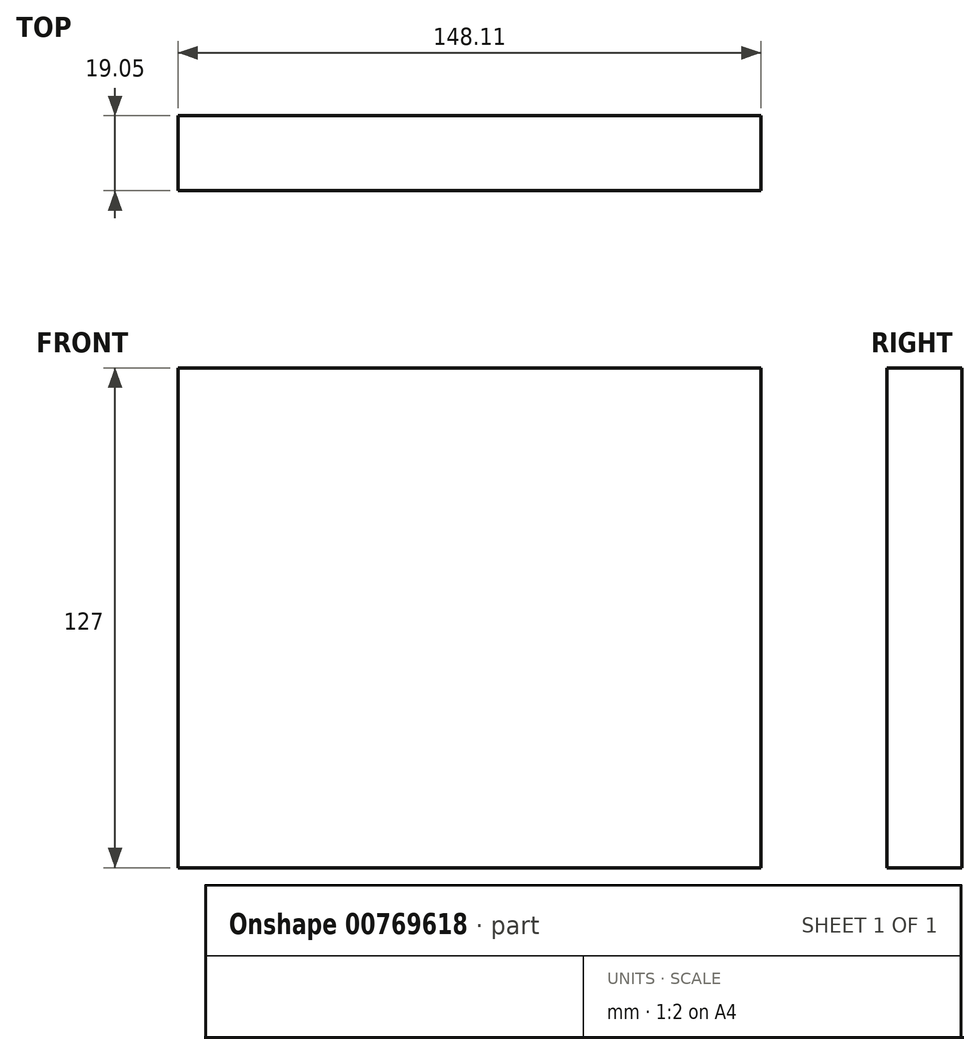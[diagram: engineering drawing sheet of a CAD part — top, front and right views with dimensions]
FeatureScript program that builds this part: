
annotation { "Feature Type Name" : "Feature", "Feature Type Description" : "" }
export const myFeature = defineFeature(function(context is Context, id is Id, definition is map)
    precondition{}
    {
        {
            var Q0;
            Q0=qCreatedBy(makeId("Front.planeOp"),FACE);
            var sketch = newSketch(context, id + "F0", { "sketchPlane" : qUnion([Q0])});
            skLineSegment(sketch, "E0.bottom", {"start": v(-78.1, 47.94) * mm, "end": v(70, 47.94) * mm});
            skLineSegment(sketch, "E0.top", {"start": v(-78.1, -79.06) * mm, "end": v(70, -79.06) * mm});
            skLineSegment(sketch, "E0.left", {"start": v(-78.1, 47.94) * mm, "end": v(-78.1, -79.06) * mm});
            skLineSegment(sketch, "E0.right", {"start": v(70, 47.94) * mm, "end": v(70, -79.06) * mm});
            skSolve(sketch);
        }
        {
            var Q0;
            Q0=makeQuery(id+"F0.imprint","IMPRINT",FACE,{"disambiguationData":[TD([[makeQuery(id+"F0.imprint","IMPRINT",EDGE,{"derivedFrom":sQuery(id+"F0.wireOp",EDGE,"E0.bottom")}),-1.0]])]});
            extrude(context, id + "F1", {"entities" : qUnion([Q0]), "depth" : 19.05 * mm, "offsetDistance" : 25.4 * mm});
        }
    });
